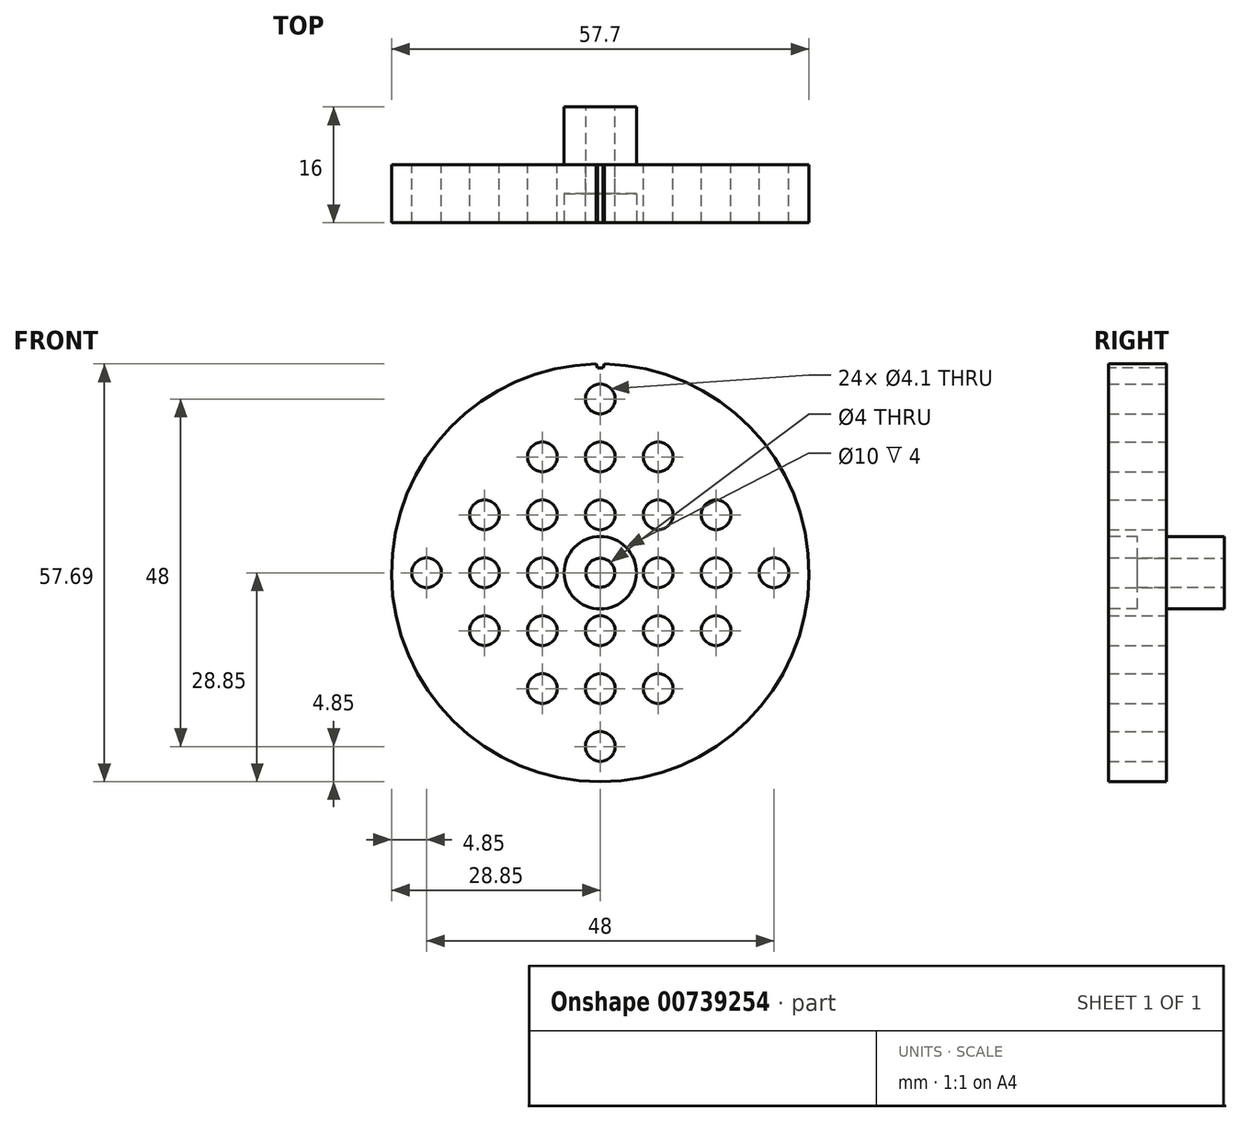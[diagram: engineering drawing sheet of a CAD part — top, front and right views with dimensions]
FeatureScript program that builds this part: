
annotation { "Feature Type Name" : "Feature", "Feature Type Description" : "" }
export const myFeature = defineFeature(function(context is Context, id is Id, definition is map)
    precondition{}
    {
        {
            var Q0;
            Q0=qCreatedBy(makeId("Front.planeOp"),FACE);
            var sketch = newSketch(context, id + "F0", { "sketchPlane" : qUnion([Q0])});
            skCircle(sketch, "E0", {"center": v(0, 0) * mm, "radius": 28.85 * mm});
            skCircle(sketch, "E1", {"center": v(-16, 0) * mm, "radius": 2.05 * mm});
            skCircle(sketch, "E2", {"center": v(-8, 0) * mm, "radius": 2.05 * mm});
            skCircle(sketch, "E3", {"center": v(-8, 8) * mm, "radius": 2.05 * mm});
            skCircle(sketch, "E4", {"center": v(0, 16) * mm, "radius": 2.05 * mm});
            skCircle(sketch, "E5", {"center": v(0, 8) * mm, "radius": 2.05 * mm});
            skCircle(sketch, "E6.MirrorC", {"center": v(8, 0) * mm, "radius": 2.05 * mm});
            skCircle(sketch, "E7.MirrorC", {"center": v(8, 8) * mm, "radius": 2.05 * mm});
            skCircle(sketch, "E8.MirrorC", {"center": v(16, 0) * mm, "radius": 2.05 * mm});
            skCircle(sketch, "E9.MirrorC", {"center": v(-8, -8) * mm, "radius": 2.05 * mm});
            skCircle(sketch, "E10.MirrorC", {"center": v(0, -8) * mm, "radius": 2.05 * mm});
            skCircle(sketch, "E11.MirrorC", {"center": v(8, -8) * mm, "radius": 2.05 * mm});
            skCircle(sketch, "E12.MirrorC", {"center": v(0, -16) * mm, "radius": 2.05 * mm});
            skCircle(sketch, "E13", {"center": v(0, 0) * mm, "radius": 2 * mm});
            skCircle(sketch, "E14", {"center": v(0, 24) * mm, "radius": 2.05 * mm});
            skCircle(sketch, "E15", {"center": v(8, 16) * mm, "radius": 2.05 * mm});
            skCircle(sketch, "E16", {"center": v(16, 8) * mm, "radius": 2.05 * mm});
            skCircle(sketch, "E17", {"center": v(24, 0) * mm, "radius": 2.05 * mm});
            skCircle(sketch, "E18.MirrorC", {"center": v(16, -8) * mm, "radius": 2.05 * mm});
            skCircle(sketch, "E19.MirrorC", {"center": v(8, -16) * mm, "radius": 2.05 * mm});
            skCircle(sketch, "E20.MirrorC", {"center": v(0, -24) * mm, "radius": 2.05 * mm});
            skCircle(sketch, "E21.MirrorC", {"center": v(-8, -16) * mm, "radius": 2.05 * mm});
            skCircle(sketch, "E22.MirrorC", {"center": v(-16, -8) * mm, "radius": 2.05 * mm});
            skCircle(sketch, "E23.MirrorC", {"center": v(-24, 0) * mm, "radius": 2.05 * mm});
            skCircle(sketch, "E24.MirrorC", {"center": v(-16, 8) * mm, "radius": 2.05 * mm});
            skCircle(sketch, "E25.MirrorC", {"center": v(-8, 16) * mm, "radius": 2.05 * mm});
            skSolve(sketch);
        }
        {
            var Q0;
            Q0=makeQuery(id+"F0.imprint","IMPRINT",FACE,{"disambiguationData":[TD([[makeQuery(id+"F0.imprint","IMPRINT",EDGE,{"derivedFrom":sQuery(id+"F0.wireOp",EDGE,"E0")}),1.0]])]});
            extrude(context, id + "F1", {"entities" : qUnion([Q0]), "endBound" : BoundingType.SYMMETRIC, "depth" : 8 * mm, "offsetDistance" : 25.4 * mm});
        }
        {
            var Q0;
            Q0=makeQuery(id+"F1.opExtrude","CAP_FACE",FACE,{"disambiguationData":[OSD([sQuery(id+"F0.wireOp",EDGE,"E0"),sQuery(id+"F0.wireOp",EDGE,"E1"),sQuery(id+"F0.wireOp",EDGE,"E2"),sQuery(id+"F0.wireOp",EDGE,"E3"),sQuery(id+"F0.wireOp",EDGE,"E4"),sQuery(id+"F0.wireOp",EDGE,"E5"),sQuery(id+"F0.wireOp",EDGE,"E6.MirrorC"),sQuery(id+"F0.wireOp",EDGE,"E7.MirrorC"),sQuery(id+"F0.wireOp",EDGE,"E8.MirrorC"),sQuery(id+"F0.wireOp",EDGE,"E9.MirrorC"),sQuery(id+"F0.wireOp",EDGE,"E10.MirrorC"),sQuery(id+"F0.wireOp",EDGE,"E11.MirrorC"),sQuery(id+"F0.wireOp",EDGE,"E12.MirrorC"),sQuery(id+"F0.wireOp",EDGE,"E13")])],"isStart":false});
            var sketch = newSketch(context, id + "F2", { "sketchPlane" : qUnion([Q0])});
            skCircle(sketch, "E26", {"center": v(0, 0) * mm, "radius": 5 * mm});
            skSolve(sketch);
        }
        {
            var Q0;
            Q0=qSketchRegion(id+"F2",true);
            extrude(context, id + "F3", {"entities" : qUnion([Q0]), "operationType" : NewBodyOperationType.REMOVE, "oppositeDirection" : true, "depth" : 4 * mm, "offsetDistance" : 25.4 * mm});
        }
        {
            var Q0;
            Q0=makeQuery(id+"F1.opExtrude","CAP_FACE",FACE,{"disambiguationData":[OSD([sQuery(id+"F0.wireOp",EDGE,"E0"),sQuery(id+"F0.wireOp",EDGE,"E1"),sQuery(id+"F0.wireOp",EDGE,"E2"),sQuery(id+"F0.wireOp",EDGE,"E3"),sQuery(id+"F0.wireOp",EDGE,"E4"),sQuery(id+"F0.wireOp",EDGE,"E5"),sQuery(id+"F0.wireOp",EDGE,"E6.MirrorC"),sQuery(id+"F0.wireOp",EDGE,"E7.MirrorC"),sQuery(id+"F0.wireOp",EDGE,"E8.MirrorC"),sQuery(id+"F0.wireOp",EDGE,"E9.MirrorC"),sQuery(id+"F0.wireOp",EDGE,"E10.MirrorC"),sQuery(id+"F0.wireOp",EDGE,"E11.MirrorC"),sQuery(id+"F0.wireOp",EDGE,"E12.MirrorC"),sQuery(id+"F0.wireOp",EDGE,"E13")])],"isStart":false});
            var sketch = newSketch(context, id + "F4", { "sketchPlane" : qUnion([Q0])});
            skLineSegment(sketch, "E27", {"start": v(-1.08, 30.84) * mm, "end": v(-0.4, 28.3) * mm});
            skLineSegment(sketch, "E28", {"start": v(0.4, 28.3) * mm, "end": v(1.08, 30.84) * mm});
            skLineSegment(sketch, "E29", {"start": v(1.08, 30.84) * mm, "end": v(-1.08, 30.84) * mm});
            skArc(sketch, "E30", {"start": v(0.4, 28.3) * mm, "mid": v(0, 28.3) * mm, "end": v(-0.4, 28.3) * mm});
            skSolve(sketch);
        }
        {
            var Q0;
            Q0=qSketchRegion(id+"F4",true);
            extrude(context, id + "F5", {"entities" : qUnion([Q0]), "operationType" : NewBodyOperationType.REMOVE, "oppositeDirection" : true, "depth" : 25.4 * mm, "offsetDistance" : 25.4 * mm});
        }
        {
            var Q0;
            Q0=makeQuery(id+"F1.opExtrude","CAP_FACE",FACE,{"disambiguationData":[OSD([sQuery(id+"F0.wireOp",EDGE,"E0"),sQuery(id+"F0.wireOp",EDGE,"E1"),sQuery(id+"F0.wireOp",EDGE,"E2"),sQuery(id+"F0.wireOp",EDGE,"E3"),sQuery(id+"F0.wireOp",EDGE,"E4"),sQuery(id+"F0.wireOp",EDGE,"E5"),sQuery(id+"F0.wireOp",EDGE,"E6.MirrorC"),sQuery(id+"F0.wireOp",EDGE,"E7.MirrorC"),sQuery(id+"F0.wireOp",EDGE,"E8.MirrorC"),sQuery(id+"F0.wireOp",EDGE,"E9.MirrorC"),sQuery(id+"F0.wireOp",EDGE,"E10.MirrorC"),sQuery(id+"F0.wireOp",EDGE,"E11.MirrorC"),sQuery(id+"F0.wireOp",EDGE,"E12.MirrorC"),sQuery(id+"F0.wireOp",EDGE,"E13")])],"isStart":true});
            var sketch = newSketch(context, id + "F6", { "sketchPlane" : qUnion([Q0])});
            skCircle(sketch, "E31", {"center": v(0, 0) * mm, "radius": 5 * mm});
            skCircle(sketch, "E32", {"center": v(0, 0) * mm, "radius": 2 * mm});
            skSolve(sketch);
        }
        {
            var Q0;
            Q0 = qSketchRegion(id + "F6", true);
            extrude(context, id + "F7", {"entities" : qUnion([Q0]), "operationType" : NewBodyOperationType.ADD, "depth" : 8 * mm, "offsetDistance" : 25.4 * mm});
        }
    });
